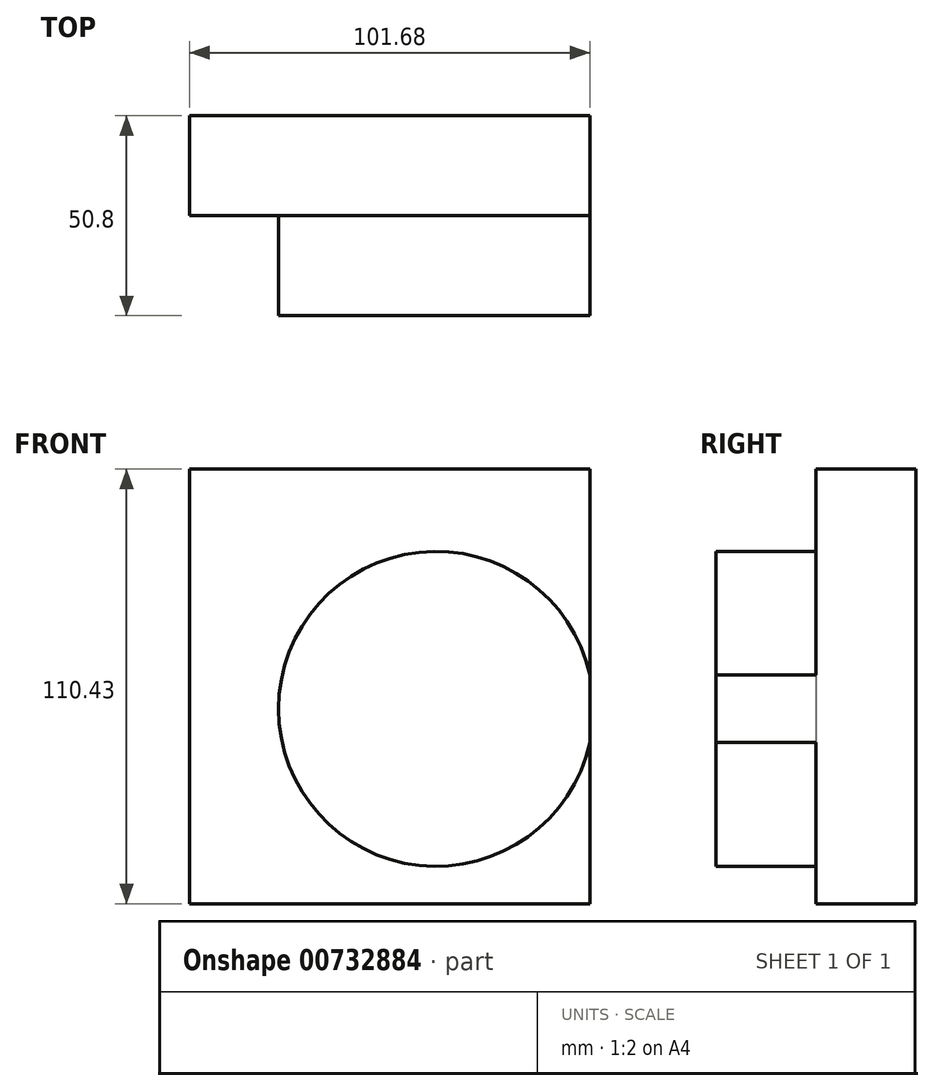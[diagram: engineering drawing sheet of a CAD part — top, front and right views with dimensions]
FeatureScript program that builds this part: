
annotation { "Feature Type Name" : "Feature", "Feature Type Description" : "" }
export const myFeature = defineFeature(function(context is Context, id is Id, definition is map)
    precondition{}
    {
        {
            var Q0;
            Q0=qCreatedBy(makeId("Front.planeOp"),FACE);
            var sketch = newSketch(context, id + "F0", { "sketchPlane" : qUnion([Q0])});
            skLineSegment(sketch, "E0.bottom", {"start": v(48.46, 60.9) * mm, "end": v(-53.22, 60.9) * mm});
            skLineSegment(sketch, "E0.top", {"start": v(48.46, -49.52) * mm, "end": v(-53.22, -49.52) * mm});
            skLineSegment(sketch, "E0.left", {"start": v(48.46, 60.9) * mm, "end": v(48.46, -49.52) * mm});
            skLineSegment(sketch, "E0.right", {"start": v(-53.22, 60.9) * mm, "end": v(-53.22, -49.52) * mm});
            skSolve(sketch);
        }
        {
            var Q0;
            Q0 = qSketchRegion(id + "F0", true);
            extrude(context, id + "F1", {"entities" : qUnion([Q0]), "depth" : 25.4 * mm, "offsetDistance" : 25.4 * mm});
        }
        {
            var Q0;
            Q0=makeQuery(id+"F1.opExtrude","CAP_FACE",FACE,{"disambiguationData":[OSD([sQuery(id+"F0.wireOp",EDGE,"E0.bottom"),sQuery(id+"F0.wireOp",EDGE,"E0.top"),sQuery(id+"F0.wireOp",EDGE,"E0.left"),sQuery(id+"F0.wireOp",EDGE,"E0.right")])],"isStart":false});
            var sketch = newSketch(context, id + "F2", { "sketchPlane" : qUnion([Q0])});
            skCircle(sketch, "E1", {"center": v(9.38, 0) * mm, "radius": 40.01 * mm});
            skSolve(sketch);
        }
        {
            var Q0;
            {var subQ0=sQuery(id+"F2.wireOp",EDGE,"E1");var subQ1=makeQuery(id+"F1.opExtrude","CAP_EDGE",EDGE,{"disambiguationData":[OSD([sQuery(id+"F0.wireOp",EDGE,"E0.left")])],"isStart":false});var subQ2=makeQuery(id+"F2.imprint","INTERSECT",VERTEX,{"disambiguationData":[OD(0.0)],"derivedFrom":[subQ1,subQ0]});Q0=makeQuery(id+"F2.imprint","IMPRINT",FACE,{"disambiguationData":[TD([[makeQuery(id+"F2.imprint","IMPRINT",EDGE,{"disambiguationData":[TD([[subQ2,-1.0]])],"derivedFrom":subQ0}),1.0]])]});}
            extrude(context, id + "F3", {"entities" : qUnion([Q0]), "operationType" : NewBodyOperationType.ADD, "depth" : 25.4 * mm, "offsetDistance" : 25.4 * mm});
        }
    });
